# Revit family: 2L-R
name_source: partatom
category: Lighting Fixtures
revit_build: Autodesk Revit 2014 (Build: 20130308_1515(x64)
units: mm (PartAtom-declared; Revit-internal decimal feet)

## types (1)
- 2L-R
    Apparent Load = 12 VA
    Application = Commercial Indoor,Education, Library, Office,Public Space,Retail
    Assembly Code = D5020200
    Color Filter = 16777215
    Connector Description = Lighting Connector
    Controls-Integral sensors = Occupancy Sensor, Daylight Sensor
    Default Elevation = 48"
    Description = MOD 2 LED Recessed Direct
    Dimming Lamp Color Temperature Shift = <None>
    Dimming Protocol = 0-10V/Lutron/DALI
    Dimming Range = 1%,10%,Dim-to-Off,Tunable White,Dim-to-Warm
    Downlight diffuser = Soft Diffuse Lens
    Emit Shape Visible in Rendering = No
    Emit from Rectangle Length = 24"
    Emit from Rectangle Width = 2"
    Features = Variable Intensity technology provides specifiable lumen output/wattage
End cap design eliminates visible diffuser seams/gaps
2 SDCM color variation
SpectraSync™ Color Tuning Technology available
NX Distributed Intelligence™ wired and wireless controls capability available
    Fixture distribution = Direct
    Housing Material = Paint - Hubbell - Matte White
    Lamp = LED
    Load Classification = Lighting
    Manufacturer = LITECONTROL
    Max Length in Row = 2L-R-D : 04
    Model = 2L-R-D
    Photometric Note = For more ies file please find the above Photometric Web Link
    Photometric Web File = 2L-R-D-4-SOF-X-CX-35K-D030.ies
    Photometric Web Link = https://www.hubbell.com
    Power Factor = 1
    Product Doucmentation Link = https://hubbellcdn.com
    Product Page URL = https://www.hubbell.com
    Reflector Finish = Hubbell - White Glass
    Tilt Angle = -90.00°
    URL = https://www.hubbell.com
    Voltage = 120 V
    Warranty = 5 years Warranty
    Wattage Comments = Variable Intensity technology provides specifiable lumen output/wattage
    Watts = 12 W

## geometry (parser evidence)
native form markers: Blend x23, Sweep x1
no freeform markers — native parametric forms only
